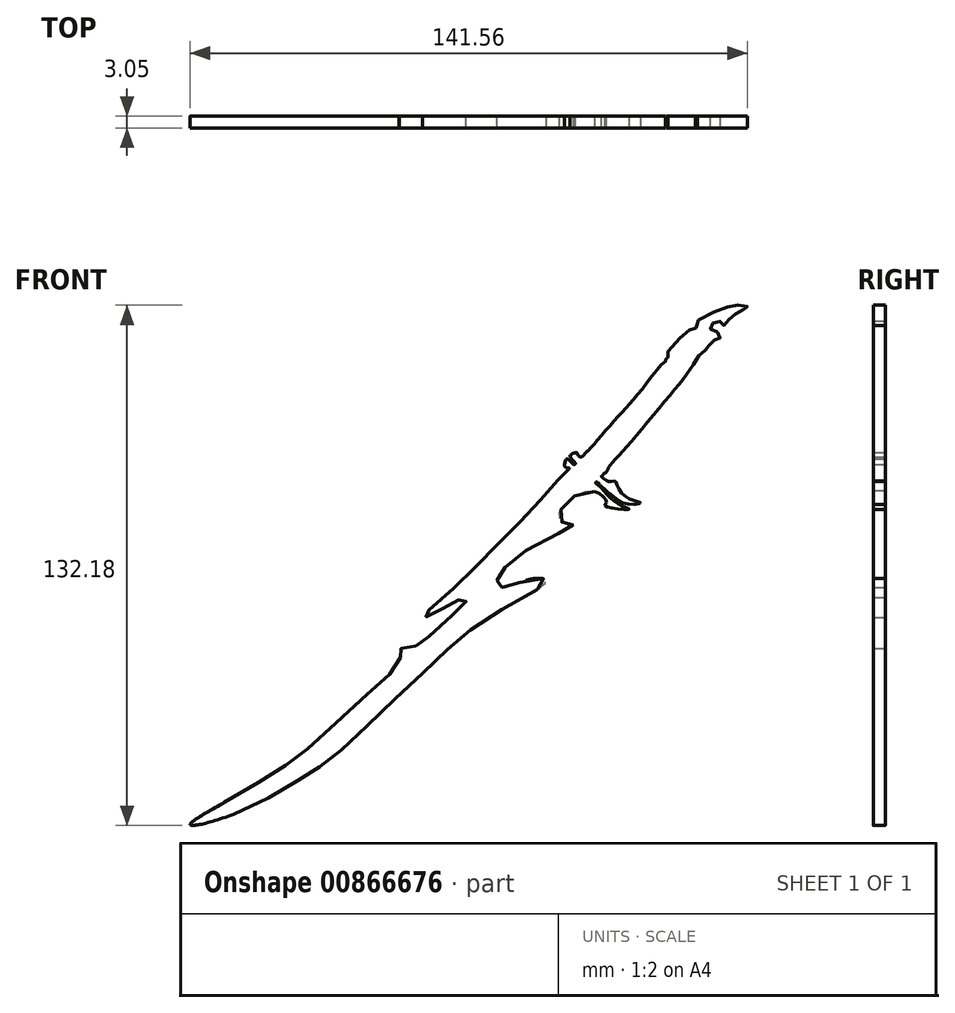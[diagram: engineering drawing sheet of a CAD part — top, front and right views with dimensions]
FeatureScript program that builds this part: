
annotation { "Feature Type Name" : "Feature", "Feature Type Description" : "" }
export const myFeature = defineFeature(function(context is Context, id is Id, definition is map)
    precondition{}
    {
        {
            var Q0;
            Q0=qCreatedBy(makeId("Front.planeOp"),FACE);
            var sketch = newSketch(context, id + "F0", { "sketchPlane" : qUnion([Q0])});
            skFitSpline(sketch, "E0", {"points": [v(-10.17, -13.09) * mm, v(-8.85, -12.85) * mm, v(-4.78, -10.77) * mm, v(-1.32, -8.84) * mm, v(0, -8.09) * mm, v(0.91, -8.96) * mm, v(-1.05, -11.2) * mm, v(-9.15, -18.51) * mm, v(-11.56, -20.17) * mm, v(-13.9, -20.98) * mm, v(-16.1, -21.1) * mm, v(-15.79, -22.2) * mm, v(-16.9, -25.7) * mm, v(-23.11, -31.75) * mm, v(-38.28, -45.55) * mm, v(-46.2, -51.52) * mm, v(-60.52, -60.14) * mm, v(-69.2, -65.8) * mm, v(-58.23, -63.16) * mm, v(-41.24, -54.24) * mm, v(-33.16, -48.82) * mm, v(-19.79, -36.4) * mm, v(-4.96, -22.43) * mm, v(6.96, -12.9) * mm, v(21.3, -3.87) * mm, v(16.85, -3.5) * mm, v(10.34, -5.56) * mm, v(9.13, -4.6) * mm, v(8.77, -3.87) * mm, v(9.86, -1.58) * mm, v(17.57, 4.69) * mm, v(28.17, 10.23) * mm, v(26.97, 10.35) * mm, v(25.16, 11.2) * mm, v(24.68, 13.48) * mm, v(27.7, 17.1) * mm, v(33.48, 18.9) * mm, v(36.63, 16.12) * mm, v(36.2, 15.55) * mm, v(37.34, 14.76) * mm, v(42.36, 14.33) * mm, v(40.14, 15.33) * mm, v(36.2, 18.7) * mm, v(33.98, 20.92) * mm, v(33.73, 21.16) * mm, v(34.28, 21.18) * mm, v(34.84, 20.65) * mm, v(36.16, 19.33) * mm, v(38.82, 17.2) * mm, v(39.83, 16.44) * mm, v(42.31, 15.6) * mm, v(45.28, 15.94) * mm, v(42.52, 16.95) * mm, v(40.21, 18.78) * mm, v(39.1, 20.78) * mm, v(38.9, 21.46) * mm, v(38.03, 21.4) * mm, v(36.9, 21.44) * mm, v(36.51, 21.66) * mm, v(35.3, 22.63) * mm, v(35.5, 22.9) * mm, v(35.83, 23.34) * mm, v(36.2, 23.46) * mm, v(36.94, 24.5) * mm, v(37.07, 24.96) * mm, v(38.68, 26.84) * mm, v(43.52, 32.32) * mm, v(52.9, 43.57) * mm, v(57.95, 50.09) * mm, v(60.64, 53.96) * mm, v(61.21, 54.13) * mm, v(62.23, 55.55) * mm, v(62.6, 55.9) * mm, v(63.68, 57.14) * mm, v(65, 57.53) * mm, v(65.49, 58.1) * mm, v(64.77, 59.34) * mm, v(63.08, 60.03) * mm, v(63.17, 61) * mm, v(64.5, 62.05) * mm, v(65.82, 61.81) * mm, v(66.3, 61.06) * mm, v(67.3, 62.11) * mm, v(68.83, 63.65) * mm, v(71, 64.94) * mm, v(72.23, 65.5) * mm, v(72.28, 65.94) * mm, v(69.18, 66.1) * mm, v(65.35, 65.1) * mm, v(59.17, 61.66) * mm, v(59.53, 61.1) * mm, v(59.65, 60.7) * mm, v(59.4, 60.39) * mm, v(58.25, 60.14) * mm, v(56.27, 58.83) * mm, v(51.79, 53.33) * mm, v(52.2, 52.93) * mm, v(51.52, 52.3) * mm, v(51.6, 51.95) * mm, v(51.13, 51.6) * mm, v(45, 44.11) * mm, v(40.27, 38.7) * mm, v(35.2, 32.96) * mm, v(31.97, 29.3) * mm, v(31.45, 28.91) * mm, v(30.39, 27.72) * mm, v(29.58, 27.85) * mm, v(29.07, 28.65) * mm, v(28.39, 28.61) * mm, v(27.36, 27.89) * mm, v(28.51, 26.27) * mm, v(28.69, 25.93) * mm, v(28.3, 25.71) * mm, v(26.55, 27.08) * mm, v(26.04, 25.12) * mm, v(26.94, 24.86) * mm, v(27.15, 24.7) * mm, v(25.7, 23.24) * mm, v(20.55, 17.5) * mm, v(12.84, 9.35) * mm, v(4.21, 0.68) * mm, v(-4.89, -8.14) * mm, v(-10.17, -13.09) * mm]});
            skLineSegment(sketch, "E1", {"start": v(27.15, 24.7) * mm, "end": v(33.48, 18.9) * mm});
            skLineSegment(sketch, "E2", {"start": v(33.73, 21.16) * mm, "end": v(28.3, 25.71) * mm});
            skLineSegment(sketch, "E3", {"start": v(28.69, 25.93) * mm, "end": v(34.28, 21.18) * mm});
            skLineSegment(sketch, "E4", {"start": v(31.97, 29.3) * mm, "end": v(37.07, 24.96) * mm});
            skLineSegment(sketch, "E5", {"start": v(27.36, 27.89) * mm, "end": v(39.83, 16.44) * mm});
            skPoint(sketch, "E6.start.orphan", {"position": v(33.73, 31.2) * mm});
            skFitSpline(sketch, "E7", {"points": [v(52.2, 52.93) * mm, v(54.94, 54.31) * mm, v(57.63, 56.44) * mm, v(59.66, 57) * mm, v(60.64, 56.03) * mm, v(60.64, 53.96) * mm], "startDerivative": vector(12.28, 5.04) * mm, "endDerivative": vector(-1.58, -11.9) * mm});
            skLineSegment(sketch, "E8", {"start": v(-60.52, -60.14) * mm, "end": v(-69.2, -65.8) * mm});
            skLineSegment(sketch, "E9", {"start": v(-58.23, -63.16) * mm, "end": v(-69.2, -65.8) * mm});
            skSolve(sketch);
        }
        {
            var Q0;
            Q0 = qSketchRegion(id + "F0", true);
            extrude(context, id + "F1", {"entities" : qUnion([Q0]), "depth" : 3.05 * mm, "offsetDistance" : 25.4 * mm});
        }
    });
